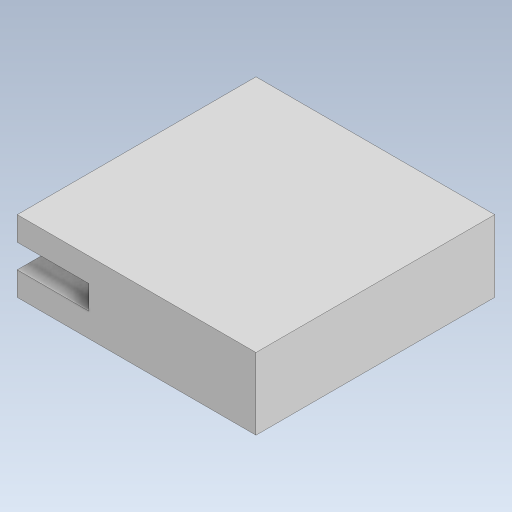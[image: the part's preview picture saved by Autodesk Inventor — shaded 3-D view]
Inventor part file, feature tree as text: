
AUTODESK INVENTOR PART (.ipt)
format: ipt  version: 2023.5 (Build 275446000, 446)  size: 108,032 bytes
history: native  units: in
note: dims shown in document units (in); Inventor stores cm internally (conversion verified against a paired STEP export)
features: extrude x3, sketch x3
ambient origin geometry x8: Origin, YZ Plane, XZ Plane, XY Plane, X Axis, Y Axis, Z Axis, Center Point
bodies: Solid1 (feature_tree)
feature tree (6):
  extrude  "Extrusion1"  Depth=0.7874in
  extrude  "Extrusion2"  Depth=0.2362in
  extrude  "Extrusion3"  Depth=0.0787in
  sketch  "Sketch1"  dims[d0=0.7874in d1=0.7874in]
  sketch  "Sketch2"  dims[d2=0.2362in d3=0.0in d4=0.2362in]
  sketch  "Sketch3"  dims[d5=0.0787in d6=0.0787in d7=0.1181in d8=0.0in d9=0.4331in d10=0.0787in d11=0.1181in d12=0.0in]
